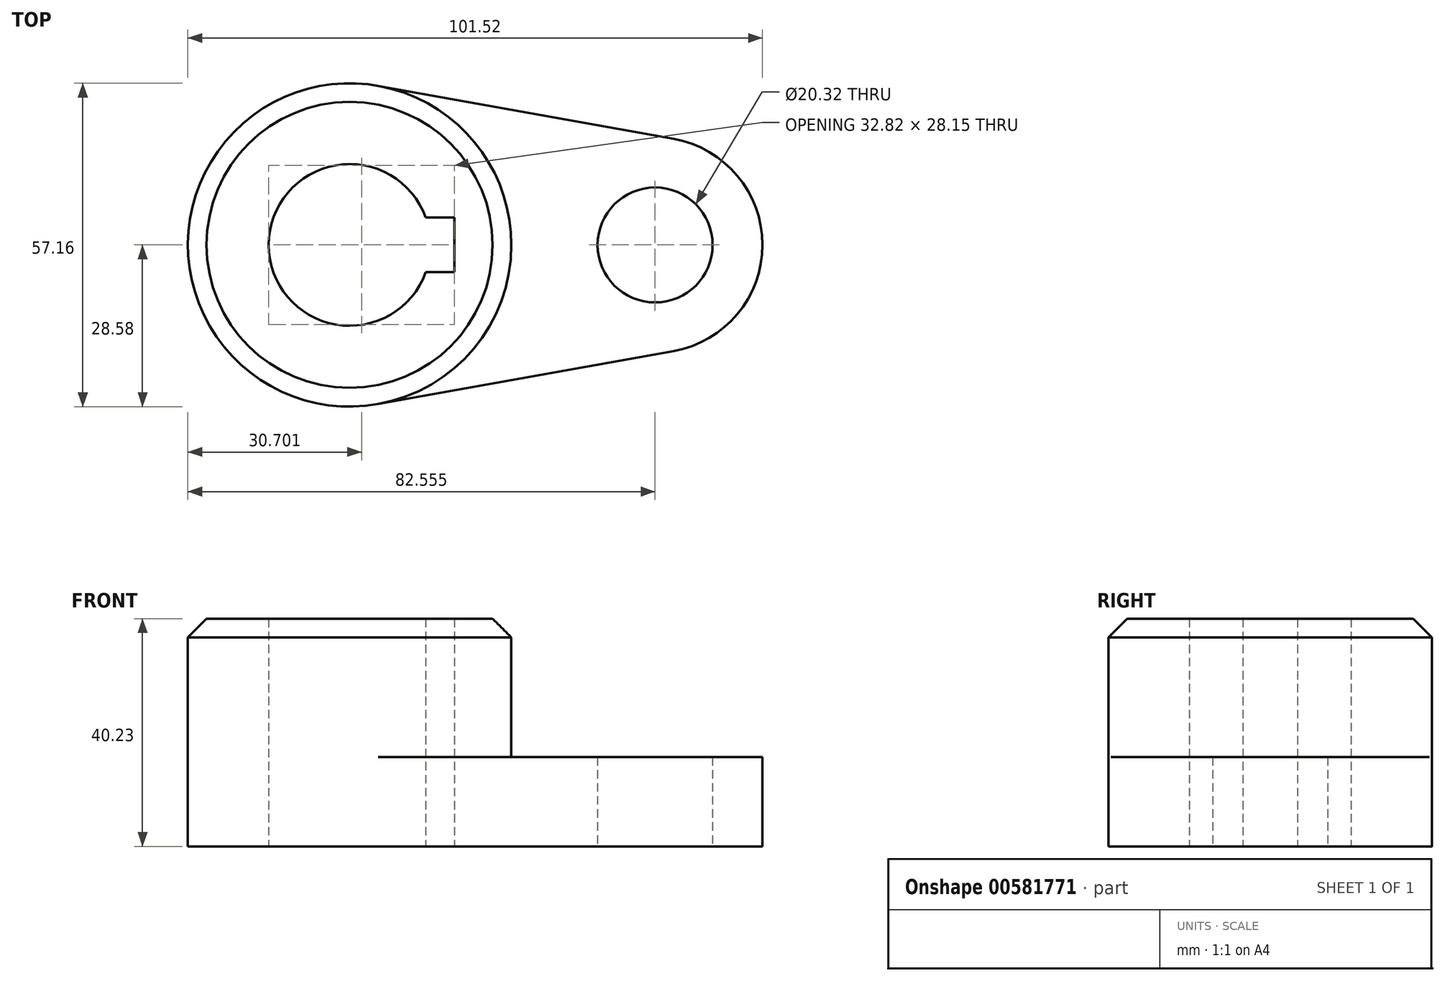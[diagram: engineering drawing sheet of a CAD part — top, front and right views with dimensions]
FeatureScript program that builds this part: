
annotation { "Feature Type Name" : "Feature", "Feature Type Description" : "" }
export const myFeature = defineFeature(function(context is Context, id is Id, definition is map)
    precondition{}
    {
        {
            var Q0;
            Q0=qCreatedBy(makeId("Top.planeOp"),FACE);
            var sketch = newSketch(context, id + "F0", { "sketchPlane" : qUnion([Q0])});
            skArc(sketch, "E0", {"start": v(13.45, 4.83) * mm, "mid": v(-14.29, 0) * mm, "end": v(13.45, -4.83) * mm});
            skCircle(sketch, "E1", {"center": v(53.98, 0) * mm, "radius": 10.16 * mm});
            skCircle(sketch, "E2", {"center": v(0, 0) * mm, "radius": 28.58 * mm});
            skLineSegment(sketch, "E3", {"start": v(0, 0) * mm, "end": v(53.98, 0) * mm, "construction": true});
            skLineSegment(sketch, "E4", {"start": v(57.26, 18.75) * mm, "end": v(5.05, 28.13) * mm});
            skLineSegment(sketch, "E5", {"start": v(57.26, -18.75) * mm, "end": v(5.05, -28.13) * mm});
            skPoint(sketch, "E6.visualSharp", {"position": v(161.68, 0) * mm});
            skArc(sketch, "E6.filletArc", {"start": v(57.26, -18.75) * mm, "mid": v(72.94, 0) * mm, "end": v(57.26, 18.75) * mm});
            skLineSegment(sketch, "E7.bottom", {"start": v(18.53, 4.83) * mm, "end": v(13.45, 4.83) * mm});
            skLineSegment(sketch, "E7.top", {"start": v(18.53, -4.83) * mm, "end": v(13.45, -4.83) * mm});
            skLineSegment(sketch, "E7.left", {"start": v(18.53, 4.83) * mm, "end": v(18.53, -4.83) * mm});
            skSolve(sketch);
        }
        {
            var Q0;
            Q0=makeQuery(id+"F0.imprint","IMPRINT",FACE,{"disambiguationData":[TD([[makeQuery(id+"F0.imprint","IMPRINT",EDGE,{"derivedFrom":sQuery(id+"F0.wireOp",EDGE,"E0")}),-1.0]])]});
            extrude(context, id + "F1", {"entities" : qUnion([Q0]), "depth" : 40.23 * mm, "offsetDistance" : 25.4 * mm});
        }
        {
            var Q0;
            Q0=makeQuery(id+"F0.imprint","IMPRINT",FACE,{"disambiguationData":[TD([[makeQuery(id+"F0.imprint","IMPRINT",EDGE,{"derivedFrom":sQuery(id+"F0.wireOp",EDGE,"E1")}),-1.0]])]});
            extrude(context, id + "F2", {"entities" : qUnion([Q0]), "operationType" : NewBodyOperationType.ADD, "depth" : 15.77 * mm, "offsetDistance" : 25.4 * mm});
        }
        {
            var Q0;
            Q0=makeQuery(id+"F1.opExtrude","CAP_EDGE",EDGE,{"disambiguationData":[OSD([sQuery(id+"F0.wireOp",EDGE,"E2")])],"isStart":false});
            chamfer(context, id + "F3", {"entities" : qUnion([Q0]), "width" : 3.3 * mm, "tangentPropagation" : true});
        }
    });
